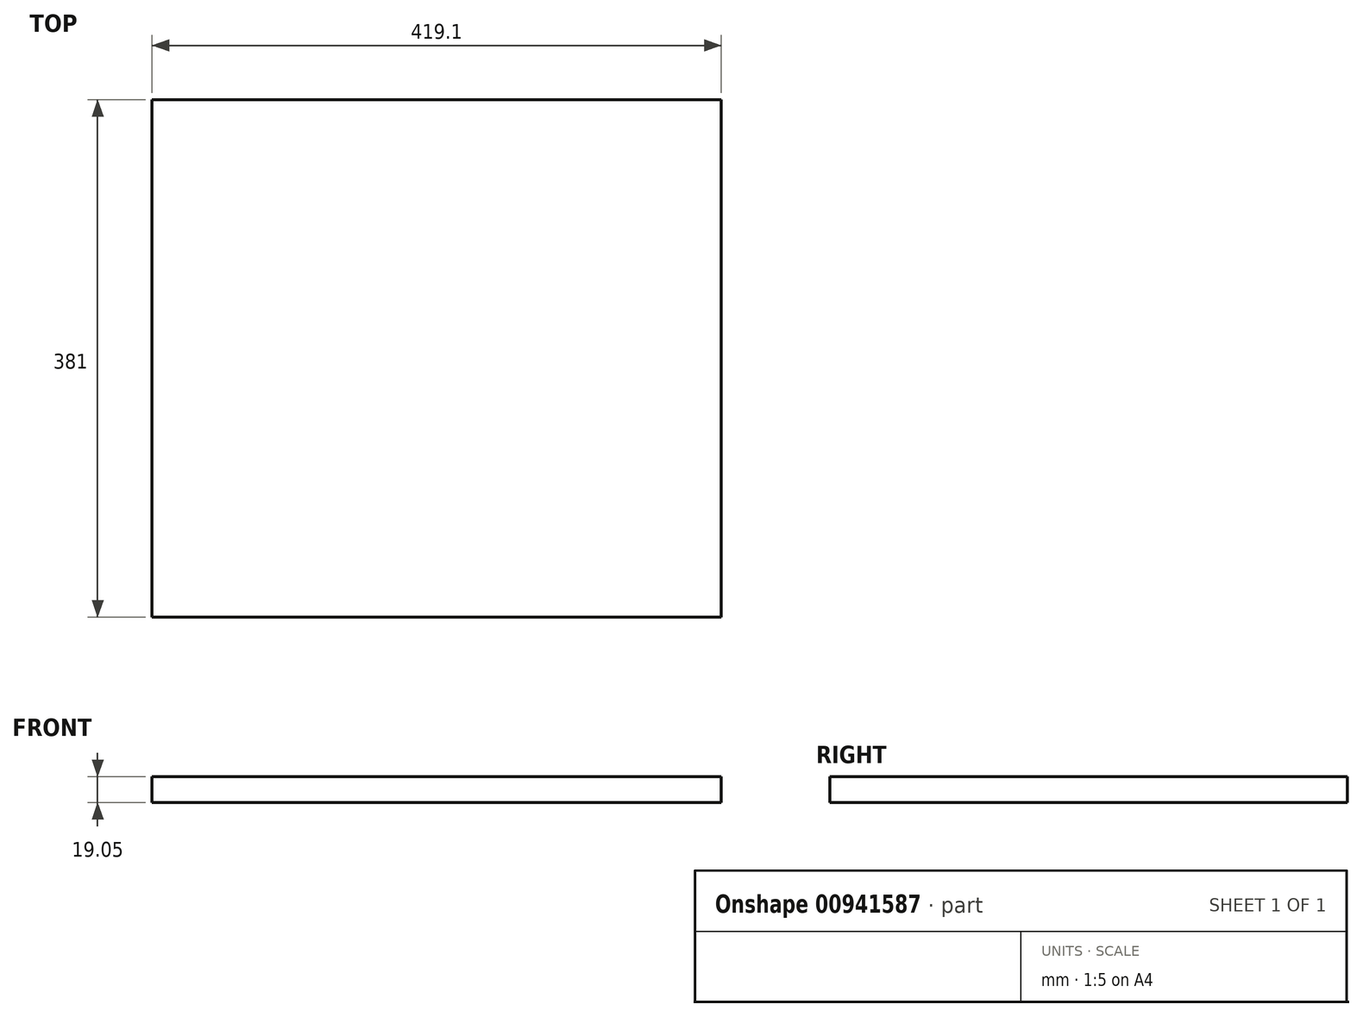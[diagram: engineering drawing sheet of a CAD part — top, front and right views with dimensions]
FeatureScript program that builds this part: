
annotation { "Feature Type Name" : "Feature", "Feature Type Description" : "" }
export const myFeature = defineFeature(function(context is Context, id is Id, definition is map)
    precondition{}
    {
        {
            var Q0;
            Q0=qCreatedBy(makeId("Front.planeOp"),FACE);
            var sketch = newSketch(context, id + "F0", { "sketchPlane" : qUnion([Q0])});
            skLineSegment(sketch, "E0.bottom", {"start": v(-200.96, 0.83) * mm, "end": v(218.14, 0.83) * mm});
            skLineSegment(sketch, "E0.top", {"start": v(-200.96, -18.22) * mm, "end": v(218.14, -18.22) * mm});
            skLineSegment(sketch, "E0.left", {"start": v(-200.96, 0.83) * mm, "end": v(-200.96, -18.22) * mm});
            skLineSegment(sketch, "E0.right", {"start": v(218.14, 0.83) * mm, "end": v(218.14, -18.22) * mm});
            skSolve(sketch);
        }
        {
            var Q0;
            Q0 = qSketchRegion(id + "F0", true);
            extrude(context, id + "F1", {"entities" : qUnion([Q0]), "depth" : 381 * mm, "offsetDistance" : 25.4 * mm});
        }
    });
